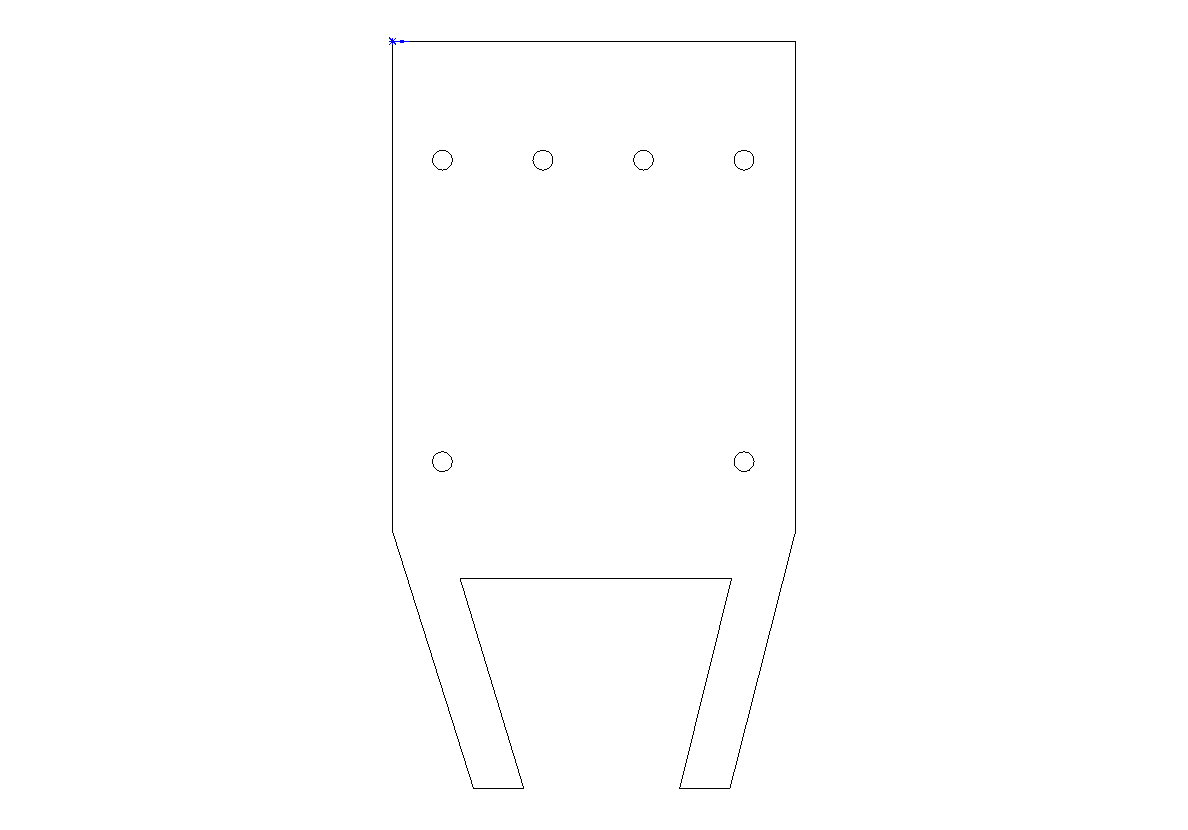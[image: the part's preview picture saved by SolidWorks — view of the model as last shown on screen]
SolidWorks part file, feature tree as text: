
SOLIDWORKS PART (.sldprt)
format: sldprt  version: not decoded by parser v0  size: 178,176 bytes
history: native  units: mm
features: sketch x3, extrude x3, material x1, pattern_linear x1 (+13 scaffold rows collapsed)
feature tree (21):
  scaffold x13  (default folders/planes/origin — collapsed)
  material  "Material <not specified>"
  sketch  "HFBR Base"  dims[D1=10.2mm D2=12.3444mm]
  extrude  "Extrude1"  Depth=7.62mm
  sketch  "Sketch2"  dims[c1.D1=6.477mm c1.D2=1.27mm c1.D3=1.27mm c1.D4=1.27mm c1.D5=6.5278mm c2.D4=6.5278mm c3.D4=~1.242818deg c4.D4=1.27mm c4.D6=1.27mm]
  extrude  "Extrude2"  Depth=7.62mm
  sketch  "Sketch3"  dims[D1=0.508mm D2=1.27mm D3=2.9972mm]
  extrude  "Pins"  Depth=3.81mm
  pattern_linear  "LPattern1"  Count1=4 Count2=2 Spacing1=2.54mm Spacing2=7.62mm
decode coverage: 7 of 7 modeling features carry decoded parameters
note: ~ marks probable driven/reference dimensions
note: suppression state not decoded; provenance and decode notes live in map.json
